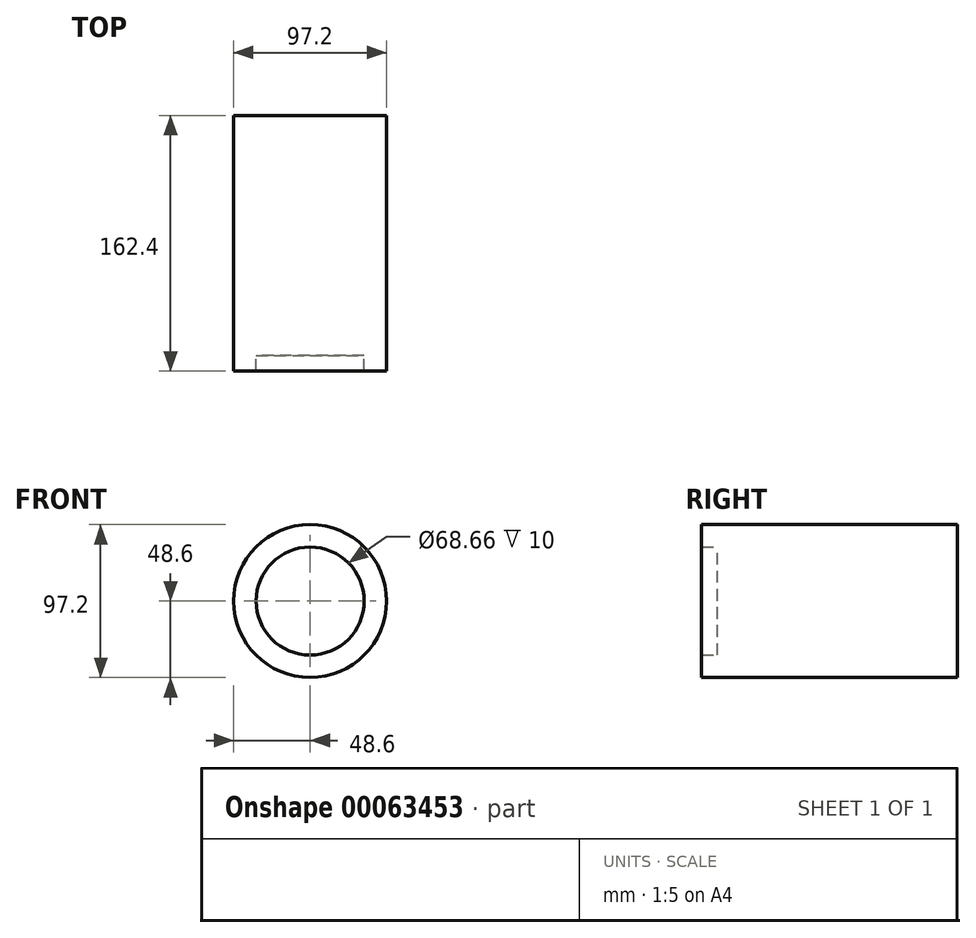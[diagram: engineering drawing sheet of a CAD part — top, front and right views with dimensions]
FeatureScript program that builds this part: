
annotation { "Feature Type Name" : "Feature", "Feature Type Description" : "" }
export const myFeature = defineFeature(function(context is Context, id is Id, definition is map)
    precondition{}
    {
        {
            var Q0;
            Q0=qCreatedBy(makeId("Front.planeOp"),FACE);
            var sketch = newSketch(context, id + "F0", { "sketchPlane" : qUnion([Q0])});
            skCircle(sketch, "E0", {"center": v(0, 0) * mm, "radius": 34.33 * mm});
            skCircle(sketch, "E1", {"center": v(0, 0) * mm, "radius": 48.6 * mm});
            skSolve(sketch);
        }
        {
            var Q0;
            Q0=makeQuery(id+"F0.imprint","IMPRINT",FACE,{"disambiguationData":[TD([[makeQuery(id+"F0.imprint","IMPRINT",EDGE,{"derivedFrom":sQuery(id+"F0.wireOp",EDGE,"E0")}),-1.0]])]});
            extrude(context, id + "F1", {"entities" : qUnion([Q0]), "depth" : 10 * mm});
        }
        {
            var Q0;
            Q0=makeQuery(id+"F1.opExtrude","CAP_FACE",FACE,{"disambiguationData":[OSD([sQuery(id+"F0.wireOp",EDGE,"E0"),sQuery(id+"F0.wireOp",EDGE,"E1")])],"isStart":true});
            var sketch = newSketch(context, id + "F2", { "sketchPlane" : qUnion([Q0])});
            skCircle(sketch, "E2", {"center": v(4.43, 218.99) * mm, "radius": 34.62 * mm});
            skCircle(sketch, "E3", {"center": v(4.43, 218.99) * mm, "radius": 41.63 * mm});
            skSolve(sketch);
        }
        {
            var Q0;
            Q0=makeQuery(id+"F2.imprint","IMPRINT",FACE,{"disambiguationData":[TD([[makeQuery(id+"F2.imprint","IMPRINT",EDGE,{"derivedFrom":makeQuery(id+"F1.opExtrude","CAP_EDGE",EDGE,{"disambiguationData":[OSD([sQuery(id+"F0.wireOp",EDGE,"E0")])],"isStart":true})}),-1.0]])]});
            var Q1;
            Q1=makeQuery(id+"F2.imprint","IMPRINT",FACE,{"disambiguationData":[TD([[makeQuery(id+"F2.imprint","IMPRINT",EDGE,{"derivedFrom":makeQuery(id+"F1.opExtrude","CAP_EDGE",EDGE,{"disambiguationData":[OSD([sQuery(id+"F0.wireOp",EDGE,"E0")])],"isStart":true})}),1.0]])]});
            extrude(context, id + "F3", {"entities" : qUnion([Q0, Q1]), "operationType" : NewBodyOperationType.ADD, "depth" : 152.4 * mm});
        }
    });
